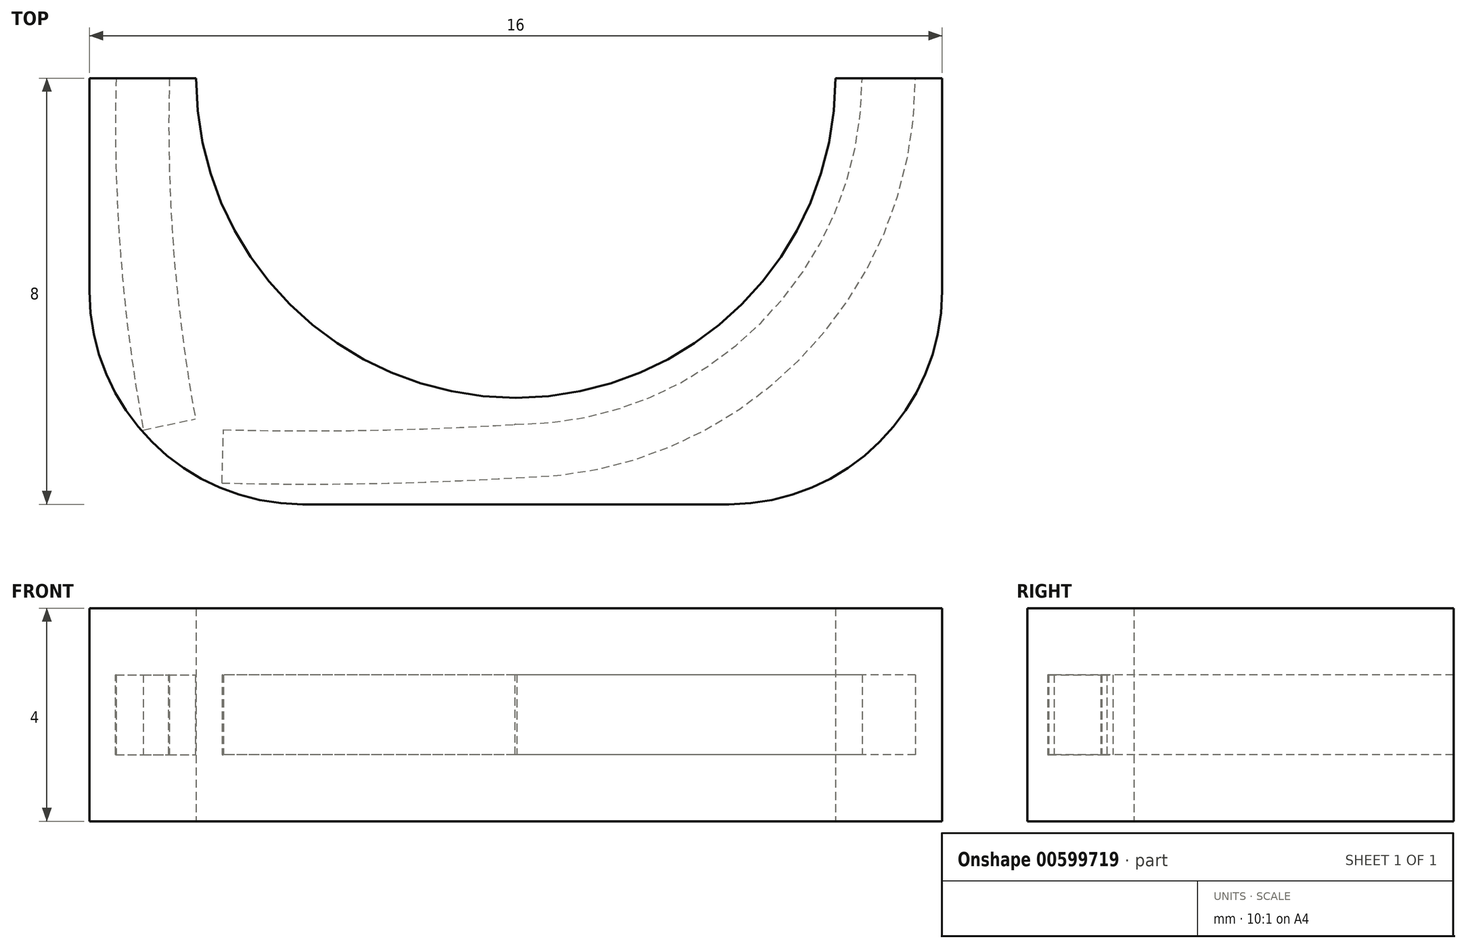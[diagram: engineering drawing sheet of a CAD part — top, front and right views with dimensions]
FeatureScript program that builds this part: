
annotation { "Feature Type Name" : "Feature", "Feature Type Description" : "" }
export const myFeature = defineFeature(function(context is Context, id is Id, definition is map)
    precondition{}
    {
        {
            var Q0;
            Q0=qCreatedBy(makeId("Top.planeOp"),FACE);
            var sketch = newSketch(context, id + "F0", { "sketchPlane" : qUnion([Q0])});
            skLineSegment(sketch, "E0.bottom", {"start": v(0, 0) * mm, "end": v(16, 0) * mm});
            skLineSegment(sketch, "E0.top", {"start": v(0, 8) * mm, "end": v(2, 8) * mm});
            skLineSegment(sketch, "E0.left", {"start": v(0, 0) * mm, "end": v(0, 8) * mm});
            skLineSegment(sketch, "E0.right", {"start": v(16, 0) * mm, "end": v(16, 8) * mm});
            skPoint(sketch, "E1", {"position": v(8, 8) * mm});
            skArc(sketch, "E2", {"start": v(2, 8) * mm, "mid": v(8, 2) * mm, "end": v(14, 8) * mm});
            skLineSegment(sketch, "E3.trimOffspring", {"start": v(14, 8) * mm, "end": v(16, 8) * mm});
            skSolve(sketch);
        }
        {
            var Q0;
            Q0=makeQuery(id+"F0.imprint","IMPRINT",FACE,{"disambiguationData":[TD([[makeQuery(id+"F0.imprint","IMPRINT",EDGE,{"derivedFrom":sQuery(id+"F0.wireOp",EDGE,"E0.bottom")}),1.0]])]});
            extrude(context, id + "F1", {"entities" : qUnion([Q0]), "depth" : 4 * mm, "offsetDistance" : 25 * mm});
        }
        {
            var Q0;
            Q0=makeQuery(id+"F1.opExtrude","CAP_FACE",FACE,{"disambiguationData":[OSD([sQuery(id+"F0.wireOp",EDGE,"E0.bottom"),sQuery(id+"F0.wireOp",EDGE,"E0.top"),sQuery(id+"F0.wireOp",EDGE,"E0.left"),sQuery(id+"F0.wireOp",EDGE,"E0.right"),sQuery(id+"F0.wireOp",EDGE,"E2"),sQuery(id+"F0.wireOp",EDGE,"E3.trimOffspring")])],"isStart":false});
            cPlane(context, id + "F2", {"entities" : qUnion([Q0]), "cplaneType" : CPlaneType.OFFSET, "offset" : 2 * mm, "oppositeDirection" : true, "width" : 150 * mm, "height" : 150 * mm});
        }
        {
            var Q0;
            Q0=qCreatedBy(id+"F2.planeOp",FACE);
            var sketch = newSketch(context, id + "F3", { "sketchPlane" : qUnion([Q0])});
            skPoint(sketch, "E4", {"position": v(0, 8) * mm});
            skPoint(sketch, "E5", {"position": v(8, 0) * mm});
            skPoint(sketch, "E6", {"position": v(1, 8) * mm});
            skPoint(sketch, "E7", {"position": v(1.5, 0) * mm});
            skPoint(sketch, "E8", {"position": v(1.5, 1.5) * mm});
            skArc(sketch, "E9", {"start": v(1, 8) * mm, "mid": v(1.08, 4.74) * mm, "end": v(1.5, 1.5) * mm});
            skPoint(sketch, "E10", {"position": v(8, 8) * mm});
            skPoint(sketch, "E11", {"position": v(15, 8) * mm});
            skPoint(sketch, "E12", {"position": v(2.5, 0) * mm});
            skPoint(sketch, "E13", {"position": v(2.5, 0.9) * mm});
            skArc(sketch, "E14", {"start": v(15, 8) * mm, "mid": v(12.95, 3.05) * mm, "end": v(8, 1) * mm});
            skPoint(sketch, "E15", {"position": v(8, 1) * mm});
            skArc(sketch, "E16", {"start": v(2.5, 0.9) * mm, "mid": v(5.25, 0.89) * mm, "end": v(8, 1) * mm});
            skPoint(sketch, "E17", {"position": v(0, 1.5) * mm});
            skLineSegment(sketch, "E18", {"start": v(1.5, 1.5) * mm, "end": v(2.5, 0.9) * mm});
            skLineSegment(sketch, "E19", {"start": v(2.5, 0.9) * mm, "end": v(1.96, 0) * mm});
            skLineSegment(sketch, "E20", {"start": v(1.5, 1.5) * mm, "end": v(0.6, 0) * mm});
            skLineSegment(sketch, "E21", {"start": v(0.6, 0) * mm, "end": v(1.96, 0) * mm});
            skArc(sketch, "E22", {"start": v(1.5, 1.5) * mm, "mid": v(1.94, 1.1) * mm, "end": v(2.5, 0.9) * mm});
            skSolve(sketch);
        }
        {
            var Q0;
            Q0=makeQuery(id+"F1.opExtrude","SWEPT_FACE",FACE,{"disambiguationData":[OSD([sQuery(id+"F0.wireOp",EDGE,"E0.top")])]});
            var sketch = newSketch(context, id + "F4", { "sketchPlane" : qUnion([Q0])});
            skPoint(sketch, "E23", {"position": v(-1, 2) * mm});
            skPoint(sketch, "E23.positionSnap0", {"position": v(0, 2) * mm});
            skLineSegment(sketch, "E24.bottom", {"start": v(-0.5, 2.75) * mm, "end": v(-1.5, 2.75) * mm});
            skLineSegment(sketch, "E24.top", {"start": v(-0.5, 1.25) * mm, "end": v(-1.5, 1.25) * mm});
            skLineSegment(sketch, "E24.left", {"start": v(-0.5, 2.75) * mm, "end": v(-0.5, 1.25) * mm});
            skLineSegment(sketch, "E24.right", {"start": v(-1.5, 2.75) * mm, "end": v(-1.5, 1.25) * mm});
            skPoint(sketch, "E25", {"position": v(-8, 2) * mm});
            skLineSegment(sketch, "E26", {"start": v(-8, 2) * mm, "end": v(-8, 0) * mm});
            skLineSegment(sketch, "E27.MirrorCS", {"start": v(-14.5, 2.75) * mm, "end": v(-14.5, 1.25) * mm});
            skLineSegment(sketch, "E28.MirrorCS", {"start": v(-15.5, 1.25) * mm, "end": v(-14.5, 1.25) * mm});
            skLineSegment(sketch, "E29.MirrorCS", {"start": v(-15.5, 2.75) * mm, "end": v(-15.5, 1.25) * mm});
            skLineSegment(sketch, "E30.MirrorCS", {"start": v(-15.5, 2.75) * mm, "end": v(-14.5, 2.75) * mm});
            skPoint(sketch, "E31.MirrorP", {"position": v(-15, 2) * mm});
            skSolve(sketch);
        }
        {
            var Q0;
            Q0=makeQuery(id+"F1.opExtrude","SWEPT_EDGE",EDGE,{"disambiguationData":[OSD([sQuery(id+"F0.wireOp",EDGE,"E0.bottom"),sQuery(id+"F0.wireOp",EDGE,"E0.right")])]});
            var Q1;
            Q1=makeQuery(id+"F1.opExtrude","SWEPT_EDGE",EDGE,{"disambiguationData":[OSD([sQuery(id+"F0.wireOp",EDGE,"E0.bottom"),sQuery(id+"F0.wireOp",EDGE,"E0.left")])]});
            fillet(context, id + "F5", {"entities" : qUnion([Q0, Q1]), "radius" : 4 * mm, "tangentPropagation" : true, "allowEdgeOverflow" : false});
        }
        {
            var Q0;
            Q0=makeQuery(id+"F4.imprint","IMPRINT",FACE,{"disambiguationData":[TD([[makeQuery(id+"F4.imprint","IMPRINT",EDGE,{"derivedFrom":sQuery(id+"F4.wireOp",EDGE,"E27.MirrorCS")}),-1.0]])]});
            var Q1;
            Q1=sQuery(id+"F3.wireOp",EDGE,"E14");
            var Q2;
            Q2=sQuery(id+"F3.wireOp",EDGE,"E16");
            sweep(context, id + "F6", {"operationType" : NewBodyOperationType.REMOVE, "profiles" : qUnion([Q0]), "path" : qUnion([Q1, Q2])});
        }
        {
            var Q0;
            Q0=makeQuery(id+"F4.imprint","IMPRINT",FACE,{"disambiguationData":[TD([[makeQuery(id+"F4.imprint","IMPRINT",EDGE,{"derivedFrom":sQuery(id+"F4.wireOp",EDGE,"E24.bottom")}),1.0]])]});
            var Q1;
            Q1=sQuery(id+"F3.wireOp",EDGE,"E9");
            sweep(context, id + "F7", {"operationType" : NewBodyOperationType.REMOVE, "profiles" : qUnion([Q0]), "path" : qUnion([Q1])});
        }
    });
